# Revit family: E15 Loudspeaker
name_source: partatom
category: Communication Devices
revit_build: Autodesk Revit 2014 (Build: 20130308_1515(x64)
units: mm (PartAtom-declared; Revit-internal decimal feet)

## types (1)
- E15 Loudspeaker
    Coverage Horizontal = 75.00°
    Coverage Vertical = 75.00°
    Default Elevation = 0 mm
    Depth = 445 mm
    Description = 15" Two-Way Passive Loudspeaker
    Enclosure Material = Black Finish
    Grille Material = Black Grille
    Height = 716 mm
    Impedance = 8
    Manufacturer = QSC Audio Products, LLC
    Manufacturer URL = www.qsc.com
    Model = E15
    Power Handling = 500
    Power Handling 2 = 2000
    Product Documentation Link = http://www.qsc.com
    Product Page URL = http://www.qsc.com
    SPL Max = 131
    Sensitivity = 97
    URL = http://www.qsc.com
    Weight Dimensional (kg) = 34
    Weight Dimensional (lb) = 75
    Weight Product (kg) = 31
    Weight Product (lb) = 68
    Width = 420 mm

## geometry (parser evidence)
native form markers: Blend x1, Sweep x9
no freeform markers — native parametric forms only
